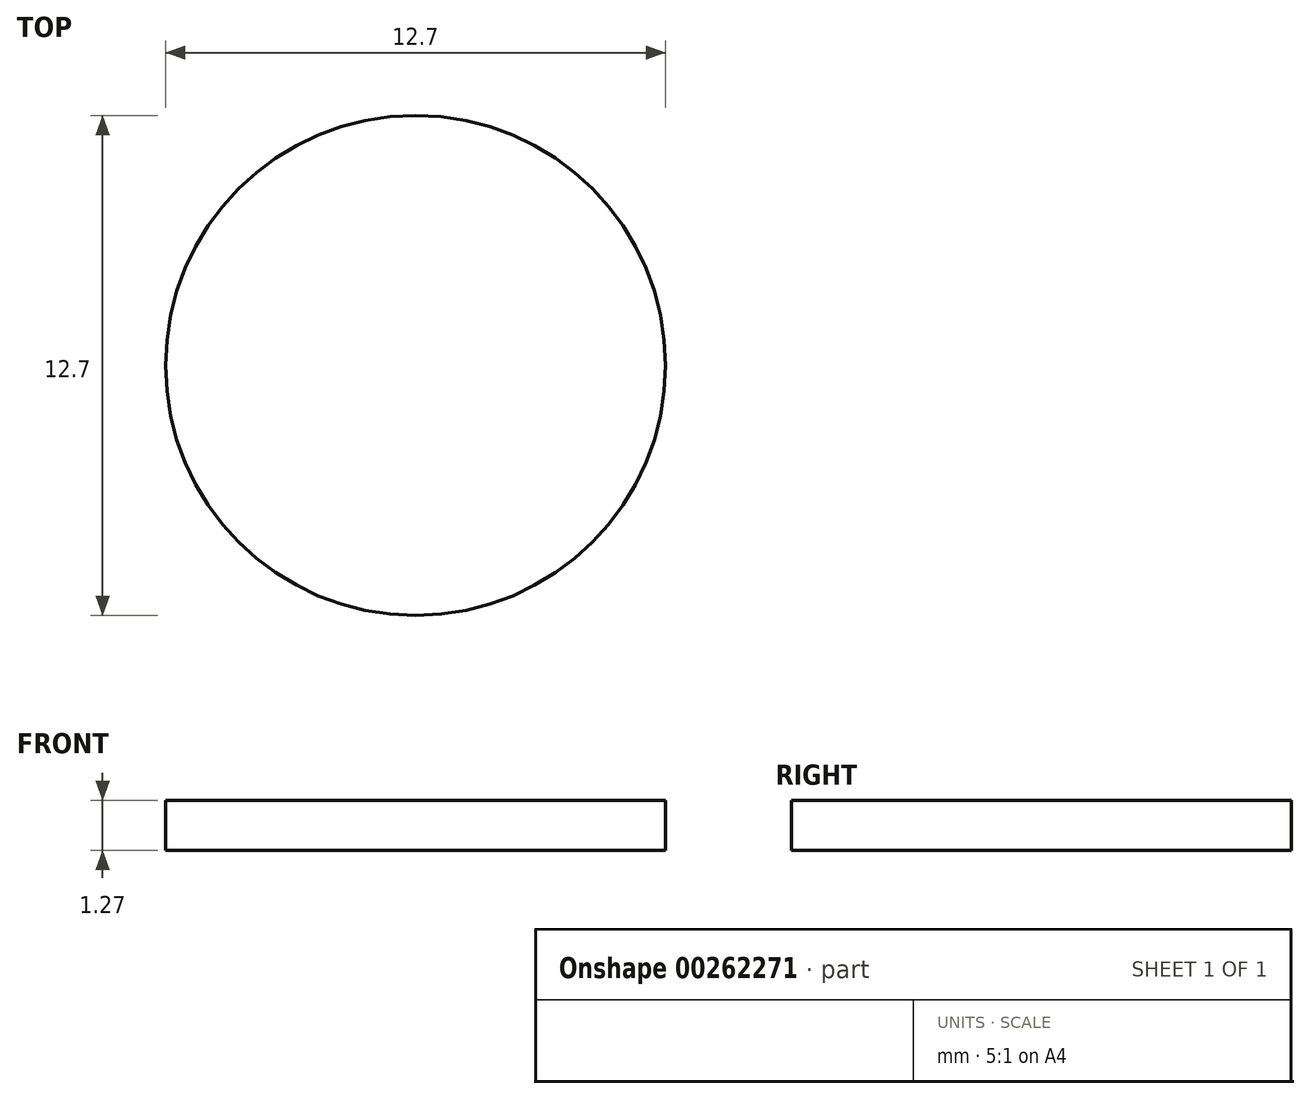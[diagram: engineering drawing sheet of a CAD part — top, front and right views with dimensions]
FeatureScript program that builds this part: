
annotation { "Feature Type Name" : "Feature", "Feature Type Description" : "" }
export const myFeature = defineFeature(function(context is Context, id is Id, definition is map)
    precondition{}
    {
        {
            var Q0;
            Q0=qCreatedBy(makeId("Top.planeOp"),FACE);
            var sketch = newSketch(context, id + "F0", { "sketchPlane" : qUnion([Q0])});
            skCircle(sketch, "E0", {"center": v(0, 0) * mm, "radius": 6.35 * mm});
            skSolve(sketch);
        }
        {
            var Q0;
            Q0=makeQuery(id+"F0.imprint","IMPRINT",FACE,{"disambiguationData":[TD([[makeQuery(id+"F0.imprint","IMPRINT",EDGE,{"derivedFrom":sQuery(id+"F0.wireOp",EDGE,"E0")}),1.0]])]});
            extrude(context, id + "F1", {"entities" : qUnion([Q0]), "depth" : 1.27 * mm});
        }
    });
